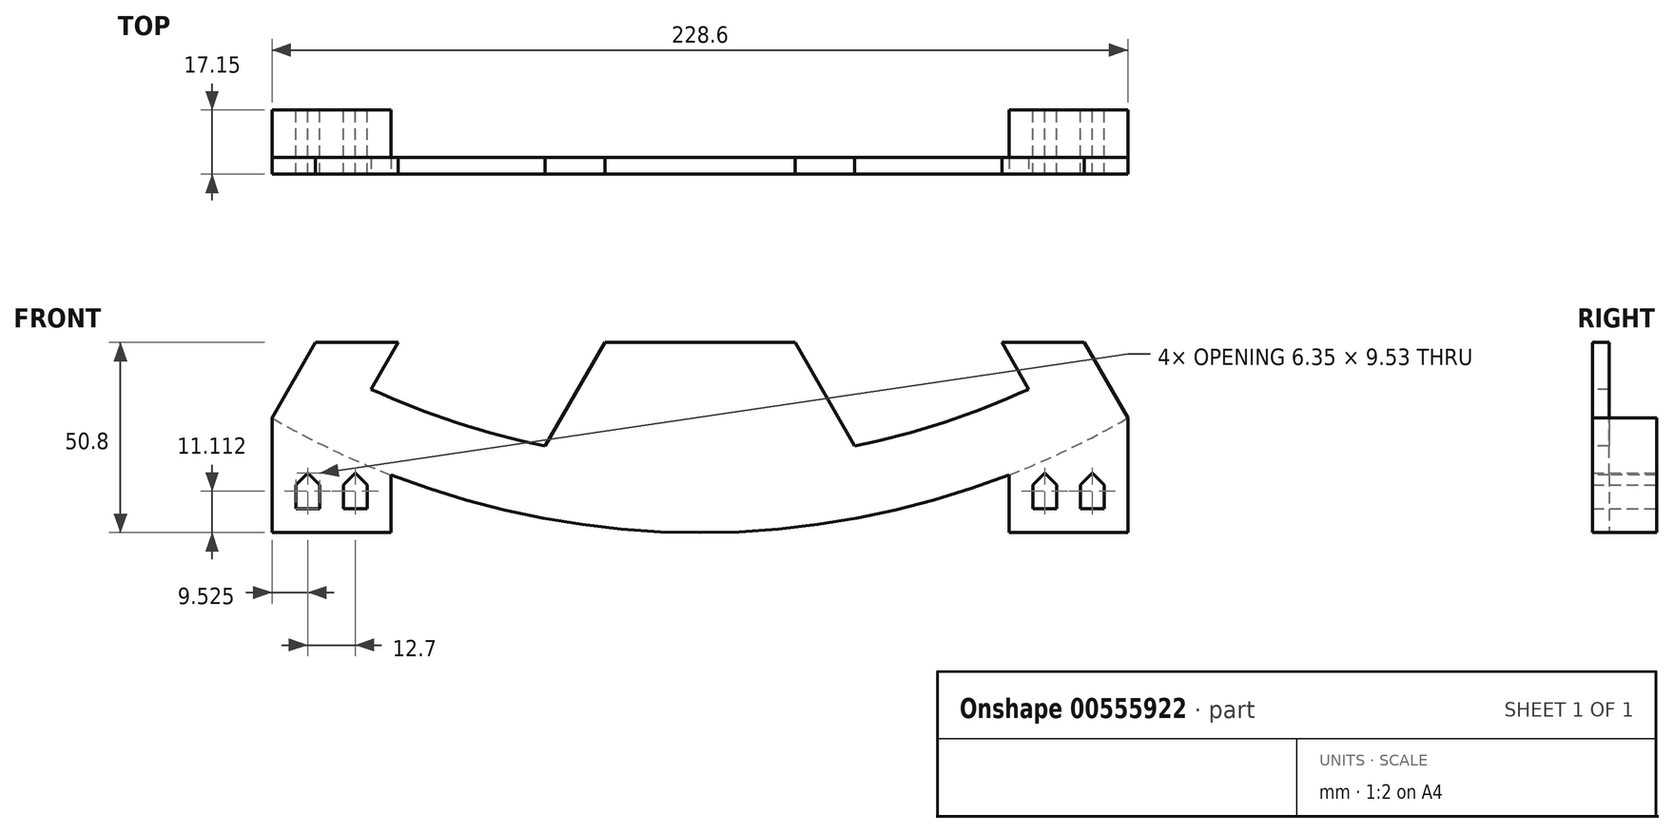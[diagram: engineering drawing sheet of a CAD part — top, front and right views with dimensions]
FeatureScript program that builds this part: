
annotation { "Feature Type Name" : "Feature", "Feature Type Description" : "" }
export const myFeature = defineFeature(function(context is Context, id is Id, definition is map)
    precondition{}
    {
        {
            var Q0;
            Q0=qCreatedBy(makeId("Front.planeOp"),FACE);
            var sketch = newSketch(context, id + "F0", { "sketchPlane" : qUnion([Q0])});
            skArc(sketch, "E0", {"start": v(-228.6, 0) * mm, "mid": v(0, -228.6) * mm, "end": v(228.6, 0) * mm});
            skLineSegment(sketch, "E1", {"start": v(-38.1, 0) * mm, "end": v(-228.6, 0) * mm});
            skLineSegment(sketch, "E2", {"start": v(38.1, 0) * mm, "end": v(228.6, 0) * mm});
            skLineSegment(sketch, "E3", {"start": v(-19.05, -33) * mm, "end": v(-114.3, -197.97) * mm});
            skLineSegment(sketch, "E4", {"start": v(19.05, -33) * mm, "end": v(114.3, -197.97) * mm});
            skArc(sketch, "E5", {"start": v(19.05, -33) * mm, "mid": v(0, 38.1) * mm, "end": v(-19.05, -33) * mm});
            skSolve(sketch);
        }
        {
            var Q0;
            {var subQ3=sQuery(id+"F0.wireOp",EDGE,"E3");Q0=makeQuery(id+"F0.imprint","IMPRINT",FACE,{"disambiguationData":[TD([[makeQuery(id+"F0.imprint","IMPRINT",EDGE,{"derivedFrom":subQ3}),1.0]])]});}
            extrude(context, id + "F1", {"entities" : qUnion([Q0]), "depth" : 127 * mm, "offsetDistance" : 25.4 * mm});
        }
        {
            var Q0;
            Q0=makeQuery(id+"F1.opExtrude","SWEPT_FACE",FACE,{"disambiguationData":[OSD([sQuery(id+"F0.wireOp",EDGE,"E5")])]});
            var Q1;
            Q1=makeQuery(id+"F1.opExtrude","SWEPT_FACE",FACE,{"disambiguationData":[OSD([sQuery(id+"F0.wireOp",EDGE,"E4")])]});
            var Q2;
            Q2=makeQuery(id+"F1.opExtrude","SWEPT_FACE",FACE,{"disambiguationData":[OSD([sQuery(id+"F0.wireOp",EDGE,"E3")])]});
            shell(context, id + "F2", {"entities" : qUnion([Q0, Q1, Q2]), "thickness" : 4.44 * mm});
        }
        {
            var Q0;
            Q0=makeQuery(id+"F1.opExtrude","CAP_FACE",FACE,{"disambiguationData":[OSD([sQuery(id+"F0.wireOp",EDGE,"E0"),sQuery(id+"F0.wireOp",EDGE,"E3"),sQuery(id+"F0.wireOp",EDGE,"E4"),sQuery(id+"F0.wireOp",EDGE,"E5")])],"isStart":false});
            var sketch = newSketch(context, id + "F3", { "sketchPlane" : qUnion([Q0])});
            skLineSegment(sketch, "E6.0", {"start": v(7.05, -50.3) * mm, "end": v(87.84, -190.25) * mm});
            skArc(sketch, "E6.1", {"start": v(-87.84, -190.25) * mm, "mid": v(-48.4, -203.88) * mm, "end": v(-7.05, -209.43) * mm});
            skCircle(sketch, "E7", {"center": v(0, 0) * mm, "radius": 9.53 * mm});
            skLineSegment(sketch, "E8", {"start": v(-7.05, -50.3) * mm, "end": v(-7.05, -125.9) * mm});
            skLineSegment(sketch, "E9", {"start": v(7.05, -50.3) * mm, "end": v(7.05, -125.9) * mm});
            skLineSegment(sketch, "E10", {"start": v(-87.84, -190.25) * mm, "end": v(-50.62, -125.78) * mm});
            skPoint(sketch, "E11.endSnap0", {"position": v(-66.67, -115.48) * mm});
            skLineSegment(sketch, "E12", {"start": v(-44.27, -114.78) * mm, "end": v(-14.9, -131.73) * mm});
            skLineSegment(sketch, "E13.trimOffspring", {"start": v(-7.05, -169.35) * mm, "end": v(-7.05, -209.43) * mm});
            skLineSegment(sketch, "E14.trimOffspring", {"start": v(-50.62, -125.78) * mm, "end": v(-87.84, -190.25) * mm});
            skArc(sketch, "E15.trimOffspring", {"start": v(7.05, -209.43) * mm, "mid": v(48.4, -203.88) * mm, "end": v(87.84, -190.25) * mm});
            skLineSegment(sketch, "E16", {"start": v(-7.05, -50.3) * mm, "end": v(0, -50.3) * mm, "construction": true});
            skLineSegment(sketch, "E17", {"start": v(0, -50.3) * mm, "end": v(0, -85.39) * mm, "construction": true});
            skLineSegment(sketch, "E18", {"start": v(-44.27, -114.78) * mm, "end": v(-7.05, -50.3) * mm});
            skLineSegment(sketch, "E19.MirrorCS", {"start": v(44.27, -114.78) * mm, "end": v(14.9, -131.73) * mm});
            skLineSegment(sketch, "E20.trimOffspring", {"start": v(7.05, -169.35) * mm, "end": v(7.05, -209.43) * mm});
            skArc(sketch, "E21", {"start": v(14.9, -131.73) * mm, "mid": v(11.36, -128.3) * mm, "end": v(7.05, -125.9) * mm});
            skPoint(sketch, "E22.orphan", {"position": v(7.05, -136.27) * mm});
            skPoint(sketch, "E23.orphan", {"position": v(7.05, -150.93) * mm});
            skPoint(sketch, "E24.orphan", {"position": v(-7.05, -150.93) * mm});
            skPoint(sketch, "E25.orphan", {"position": v(-7.05, -136.27) * mm});
            skLineSegment(sketch, "E26", {"start": v(50.62, -125.78) * mm, "end": v(7.05, -169.35) * mm, "construction": true});
            skLineSegment(sketch, "E27", {"start": v(50.62, -125.78) * mm, "end": v(7.05, -169.35) * mm});
            skLineSegment(sketch, "E28.MirrorCS", {"start": v(-50.62, -125.78) * mm, "end": v(-7.05, -169.35) * mm});
            skArc(sketch, "E29.trimOffspring", {"start": v(-7.05, -125.9) * mm, "mid": v(-11.36, -128.3) * mm, "end": v(-14.9, -131.73) * mm});
            skSolve(sketch);
        }
        {
            var Q0;
            Q0=makeQuery(id+"F3.imprint","IMPRINT",FACE,{"disambiguationData":[TD([[makeQuery(id+"F3.imprint","IMPRINT",EDGE,{"derivedFrom":sQuery(id+"F3.wireOp",EDGE,"E6.1")}),1.0]])]});
            var Q1;
            {var subQ2=sQuery(id+"F3.wireOp",EDGE,"E15.trimOffspring");Q1=makeQuery(id+"F3.imprint","IMPRINT",FACE,{"disambiguationData":[TD([[makeQuery(id+"F3.imprint","IMPRINT",EDGE,{"derivedFrom":subQ2}),1.0]])]});}
            var Q2;
            {var subQ0=sQuery(id+"F3.wireOp",EDGE,"E9");Q2=makeQuery(id+"F3.imprint","IMPRINT",FACE,{"disambiguationData":[TD([[makeQuery(id+"F3.imprint","IMPRINT",EDGE,{"derivedFrom":subQ0}),1.0]])]});}
            var Q3;
            {var subQ0=sQuery(id+"F3.wireOp",EDGE,"E8");Q3=makeQuery(id+"F3.imprint","IMPRINT",FACE,{"disambiguationData":[TD([[makeQuery(id+"F3.imprint","IMPRINT",EDGE,{"derivedFrom":subQ0}),-1.0]])]});}
            var Q4;
            Q4=makeQuery(id+"F3.imprint","IMPRINT",FACE,{"disambiguationData":[TD([[makeQuery(id+"F3.imprint","IMPRINT",EDGE,{"derivedFrom":sQuery(id+"F3.wireOp",EDGE,"E7")}),1.0]])]});
            var Q5;
            Q5=makeQuery(id+"F1.opExtrude","CAP_FACE",FACE,{"disambiguationData":[OSD([sQuery(id+"F0.wireOp",EDGE,"E0"),sQuery(id+"F0.wireOp",EDGE,"E3"),sQuery(id+"F0.wireOp",EDGE,"E4"),sQuery(id+"F0.wireOp",EDGE,"E5")])],"isStart":true});
            extrude(context, id + "F4", {"entities" : qUnion([Q0, Q1, Q2, Q3, Q4]), "operationType" : NewBodyOperationType.REMOVE, "endBound" : BoundingType.UP_TO_SURFACE, "oppositeDirection" : true, "depth" : 25.4 * mm, "endBoundEntityFace" : qUnion([Q5]), "offsetDistance" : 25.4 * mm});
        }
        {
            var Q0;
            Q0=qCreatedBy(makeId("Front.planeOp"),FACE);
            var sketch = newSketch(context, id + "F5", { "sketchPlane" : qUnion([Q0])});
            skLineSegment(sketch, "E30", {"start": v(0, -228.6) * mm, "end": v(114.3, -228.6) * mm});
            skLineSegment(sketch, "E31", {"start": v(0, -228.6) * mm, "end": v(-114.3, -228.6) * mm});
            skLineSegment(sketch, "E32", {"start": v(114.3, -197.97) * mm, "end": v(114.3, -228.6) * mm});
            skLineSegment(sketch, "E33", {"start": v(-114.3, -197.97) * mm, "end": v(-114.3, -228.6) * mm});
            skPoint(sketch, "E34.orphan", {"position": v(-122.47, -228.6) * mm});
            skArc(sketch, "E35.0", {"start": v(-114.3, -197.97) * mm, "mid": v(0, -228.6) * mm, "end": v(114.3, -197.97) * mm});
            skLineSegment(sketch, "E36", {"start": v(114.3, -228.6) * mm, "end": v(107.95, -228.6) * mm, "construction": true});
            skLineSegment(sketch, "E37", {"start": v(107.95, -228.6) * mm, "end": v(107.95, -222.25) * mm, "construction": true});
            skLineSegment(sketch, "E38.bottom", {"start": v(107.95, -222.25) * mm, "end": v(101.6, -222.25) * mm});
            skLineSegment(sketch, "E38.left", {"start": v(107.95, -222.25) * mm, "end": v(107.95, -215.9) * mm});
            skLineSegment(sketch, "E38.right", {"start": v(88.9, -222.25) * mm, "end": v(88.9, -215.9) * mm});
            skLineSegment(sketch, "E39", {"start": v(101.6, -222.25) * mm, "end": v(101.6, -215.9) * mm});
            skLineSegment(sketch, "E40", {"start": v(95.25, -222.25) * mm, "end": v(95.25, -215.9) * mm});
            skLineSegment(sketch, "E41.trimOffspring", {"start": v(95.25, -222.25) * mm, "end": v(88.9, -222.25) * mm});
            skLineSegment(sketch, "E42", {"start": v(104.78, -215.9) * mm, "end": v(104.78, -212.72) * mm, "construction": true});
            skLineSegment(sketch, "E43", {"start": v(92.08, -215.9) * mm, "end": v(92.08, -212.72) * mm, "construction": true});
            skLineSegment(sketch, "E44", {"start": v(107.95, -215.9) * mm, "end": v(104.78, -212.72) * mm});
            skLineSegment(sketch, "E45", {"start": v(101.6, -215.9) * mm, "end": v(104.78, -212.72) * mm});
            skLineSegment(sketch, "E46", {"start": v(95.25, -215.9) * mm, "end": v(92.08, -212.72) * mm});
            skLineSegment(sketch, "E47", {"start": v(88.9, -215.9) * mm, "end": v(92.08, -212.72) * mm});
            skLineSegment(sketch, "E48.MirrorCS", {"start": v(-104.78, -215.9) * mm, "end": v(-104.78, -212.72) * mm, "construction": true});
            skLineSegment(sketch, "E49.MirrorCS", {"start": v(-92.08, -215.9) * mm, "end": v(-92.08, -212.72) * mm, "construction": true});
            skLineSegment(sketch, "E50.MirrorCS", {"start": v(-101.6, -215.9) * mm, "end": v(-104.78, -212.72) * mm});
            skLineSegment(sketch, "E51.MirrorCS", {"start": v(-88.9, -215.9) * mm, "end": v(-92.08, -212.72) * mm});
            skLineSegment(sketch, "E52.MirrorCS", {"start": v(-107.95, -215.9) * mm, "end": v(-104.78, -212.72) * mm});
            skLineSegment(sketch, "E53.MirrorCS", {"start": v(-95.25, -222.25) * mm, "end": v(-95.25, -215.9) * mm});
            skLineSegment(sketch, "E54.MirrorCS", {"start": v(-101.6, -222.25) * mm, "end": v(-101.6, -215.9) * mm});
            skLineSegment(sketch, "E55.MirrorCS", {"start": v(-107.95, -222.25) * mm, "end": v(-107.95, -215.9) * mm});
            skLineSegment(sketch, "E56.MirrorCS", {"start": v(-107.95, -222.25) * mm, "end": v(-101.6, -222.25) * mm});
            skLineSegment(sketch, "E57.MirrorCS", {"start": v(-88.9, -222.25) * mm, "end": v(-88.9, -215.9) * mm});
            skLineSegment(sketch, "E58.MirrorCS", {"start": v(-95.25, -215.9) * mm, "end": v(-92.08, -212.72) * mm});
            skLineSegment(sketch, "E59.MirrorCS", {"start": v(-95.25, -222.25) * mm, "end": v(-88.9, -222.25) * mm});
            skSolve(sketch);
        }
        {
            var Q0;
            {var subQ2=sQuery(id+"F5.wireOp",EDGE,"E30");Q0=makeQuery(id+"F5.imprint","IMPRINT",FACE,{"disambiguationData":[TD([[makeQuery(id+"F5.imprint","IMPRINT",EDGE,{"derivedFrom":subQ2}),1.0]])]});}
            var Q1;
            {var subQ2=sQuery(id+"F5.wireOp",EDGE,"E31");Q1=makeQuery(id+"F5.imprint","IMPRINT",FACE,{"disambiguationData":[TD([[makeQuery(id+"F5.imprint","IMPRINT",EDGE,{"derivedFrom":subQ2}),-1.0]])]});}
            var Q2;
            Q2=makeQuery(id+"F1.opExtrude","CAP_FACE",FACE,{"disambiguationData":[OSD([sQuery(id+"F0.wireOp",EDGE,"E0"),sQuery(id+"F0.wireOp",EDGE,"E3"),sQuery(id+"F0.wireOp",EDGE,"E4"),sQuery(id+"F0.wireOp",EDGE,"E5")])],"isStart":false});
            extrude(context, id + "F6", {"entities" : qUnion([Q0, Q1]), "operationType" : NewBodyOperationType.ADD, "endBound" : BoundingType.UP_TO_SURFACE, "depth" : 25.4 * mm, "endBoundEntityFace" : qUnion([Q2]), "offsetDistance" : 25.4 * mm});
        }
        {
            var Q0;
            Q0=qCreatedBy(makeId("Front.planeOp"),FACE);
            var sketch = newSketch(context, id + "F7", { "sketchPlane" : qUnion([Q0])});
            skLineSegment(sketch, "E60", {"start": v(0, 0) * mm, "end": v(0, -177.8) * mm, "construction": true});
            skLineSegment(sketch, "E61", {"start": v(0, -177.8) * mm, "end": v(122.5, -177.8) * mm});
            skLineSegment(sketch, "E62", {"start": v(122.5, -177.8) * mm, "end": v(122.5, 99.95) * mm});
            skLineSegment(sketch, "E63", {"start": v(0, -177.8) * mm, "end": v(-155.13, -177.8) * mm});
            skLineSegment(sketch, "E64", {"start": v(-155.13, -177.8) * mm, "end": v(-155.13, 97.68) * mm});
            skLineSegment(sketch, "E65", {"start": v(-155.13, 97.68) * mm, "end": v(122.5, 99.95) * mm});
            skSolve(sketch);
        }
        {
            var Q0;
            Q0=makeQuery(id+"F7.imprint","IMPRINT",FACE,{"disambiguationData":[TD([[makeQuery(id+"F7.imprint","IMPRINT",EDGE,{"derivedFrom":sQuery(id+"F7.wireOp",EDGE,"E61")}),1.0]])]});
            extrude(context, id + "F8", {"entities" : qUnion([Q0]), "operationType" : NewBodyOperationType.REMOVE, "depth" : 154.94 * mm, "offsetDistance" : 25.4 * mm});
        }
        {
            var Q0;
            {var subQ0=sQuery(id+"F5.wireOp",EDGE,"E35.0");Q0=makeQuery(id+"F6.boolean.opBoolean","MERGE",FACE,{"derivedFrom":[makeQuery(id+"F1.opExtrude","CAP_FACE",FACE,{"disambiguationData":[OSD([sQuery(id+"F0.wireOp",EDGE,"E0"),sQuery(id+"F0.wireOp",EDGE,"E3"),sQuery(id+"F0.wireOp",EDGE,"E4"),sQuery(id+"F0.wireOp",EDGE,"E5")])],"isStart":true}),makeQuery(id+"F6.opExtrude","CAP_FACE",FACE,{"disambiguationData":[OSD([sQuery(id+"F5.wireOp",EDGE,"E30"),sQuery(id+"F5.wireOp",EDGE,"E32"),subQ0,sQuery(id+"F5.wireOp",EDGE,"E38.bottom"),sQuery(id+"F5.wireOp",EDGE,"E38.left"),sQuery(id+"F5.wireOp",EDGE,"E38.right"),sQuery(id+"F5.wireOp",EDGE,"E39"),sQuery(id+"F5.wireOp",EDGE,"E40"),sQuery(id+"F5.wireOp",EDGE,"E41.trimOffspring"),sQuery(id+"F5.wireOp",EDGE,"E44"),sQuery(id+"F5.wireOp",EDGE,"E45"),sQuery(id+"F5.wireOp",EDGE,"E46"),sQuery(id+"F5.wireOp",EDGE,"E47")])],"isStart":true}),makeQuery(id+"F6.opExtrude","CAP_FACE",FACE,{"disambiguationData":[OSD([sQuery(id+"F5.wireOp",EDGE,"E31"),sQuery(id+"F5.wireOp",EDGE,"E33"),subQ0,sQuery(id+"F5.wireOp",EDGE,"E50.MirrorCS"),sQuery(id+"F5.wireOp",EDGE,"E51.MirrorCS"),sQuery(id+"F5.wireOp",EDGE,"E52.MirrorCS"),sQuery(id+"F5.wireOp",EDGE,"E53.MirrorCS"),sQuery(id+"F5.wireOp",EDGE,"E54.MirrorCS"),sQuery(id+"F5.wireOp",EDGE,"E55.MirrorCS"),sQuery(id+"F5.wireOp",EDGE,"E56.MirrorCS"),sQuery(id+"F5.wireOp",EDGE,"E57.MirrorCS"),sQuery(id+"F5.wireOp",EDGE,"E58.MirrorCS"),sQuery(id+"F5.wireOp",EDGE,"E59.MirrorCS")])],"isStart":true})]});}
            var sketch = newSketch(context, id + "F9", { "sketchPlane" : qUnion([Q0])});
            skArc(sketch, "E66.0", {"start": v(-87.84, -190.25) * mm, "mid": v(-48.4, -203.88) * mm, "end": v(-7.05, -209.43) * mm});
            skLineSegment(sketch, "E67.0", {"start": v(-7.05, -209.43) * mm, "end": v(-7.05, -177.8) * mm});
            skLineSegment(sketch, "E68", {"start": v(0, -177.8) * mm, "end": v(25.4, -177.8) * mm});
            skLineSegment(sketch, "E69", {"start": v(0, -177.8) * mm, "end": v(-25.4, -177.8) * mm});
            skLineSegment(sketch, "E70", {"start": v(-25.4, -177.8) * mm, "end": v(-41.35, -205.43) * mm});
            skLineSegment(sketch, "E71", {"start": v(25.4, -177.8) * mm, "end": v(41.35, -205.43) * mm});
            skLineSegment(sketch, "E72.0", {"start": v(7.05, -209.43) * mm, "end": v(7.05, -177.8) * mm});
            skArc(sketch, "E73.0", {"start": v(7.05, -209.43) * mm, "mid": v(48.4, -203.88) * mm, "end": v(87.84, -190.25) * mm});
            skSolve(sketch);
        }
        {
            var Q0;
            {var subQ0=sQuery(id+"F9.wireOp",EDGE,"E67.0");Q0=makeQuery(id+"F9.imprint","IMPRINT",FACE,{"disambiguationData":[TD([[makeQuery(id+"F9.imprint","IMPRINT",EDGE,{"derivedFrom":subQ0}),1.0]])]});}
            var Q1;
            {var subQ2=sQuery(id+"F9.wireOp",EDGE,"E71");Q1=makeQuery(id+"F9.imprint","IMPRINT",FACE,{"disambiguationData":[TD([[makeQuery(id+"F9.imprint","IMPRINT",EDGE,{"derivedFrom":subQ2}),-1.0]])]});}
            var Q2;
            {var subQ0=sQuery(id+"F0.wireOp",EDGE,"E5");var subQ1=sQuery(id+"F0.wireOp",EDGE,"E4");var subQ2=sQuery(id+"F0.wireOp",EDGE,"E3");var subQ3=sQuery(id+"F0.wireOp",EDGE,"E0");Q2=makeQuery(id+"F2.opShell","OFFSET_FACE",FACE,{"disambiguationData":[OSD([subQ3,subQ2,subQ1,subQ0]),TDD([makeQuery(id+"F1.opExtrude","CAP_FACE",FACE,{"disambiguationData":[OSD([subQ3,subQ2,subQ1,subQ0])],"isStart":true})])]});}
            extrude(context, id + "F10", {"entities" : qUnion([Q0, Q1]), "operationType" : NewBodyOperationType.ADD, "endBound" : BoundingType.UP_TO_SURFACE, "oppositeDirection" : true, "depth" : 25.4 * mm, "endBoundEntityFace" : qUnion([Q2]), "offsetDistance" : 25.4 * mm});
        }
        {
            var Q0;
            Q0=qCreatedBy(makeId("Front.planeOp"),FACE);
            var Q1;
            {var subQ0=sQuery(id+"F0.wireOp",EDGE,"E5");var subQ1=sQuery(id+"F0.wireOp",EDGE,"E4");var subQ2=sQuery(id+"F0.wireOp",EDGE,"E3");var subQ3=sQuery(id+"F0.wireOp",EDGE,"E0");Q1=makeQuery(id+"F6.boolean.opBoolean","MERGE",FACE,{"derivedFrom":[makeQuery(id+"F1.opExtrude","CAP_FACE",FACE,{"disambiguationData":[OSD([subQ3,subQ2,subQ1,subQ0])],"isStart":false}),makeQuery(id+"F6.opExtrude","CAP_FACE",FACE,{"disambiguationData":[OSD([subQ3,subQ2,subQ1,subQ0]),OD(0.0)],"isStart":false}),makeQuery(id+"F6.opExtrude","CAP_FACE",FACE,{"disambiguationData":[OSD([subQ3,subQ2,subQ1,subQ0]),OD(1.0)],"isStart":false})]});}
            cPlane(context, id + "F11", {"entities" : qUnion([Q0, Q1]), "cplaneType" : CPlaneType.MID_PLANE, "offset" : 25.4 * mm, "width" : 152.4 * mm, "height" : 152.4 * mm});
        }
        {
            var Q0;
            Q0=makeQuery(id+"F1.opExtrude","SWEPT_BODY",BODY,{"disambiguationData":[OSD([sQuery(id+"F0.wireOp",EDGE,"E0"),sQuery(id+"F0.wireOp",EDGE,"E3"),sQuery(id+"F0.wireOp",EDGE,"E4"),sQuery(id+"F0.wireOp",EDGE,"E5")])]});
            var Q1;
            Q1=qCreatedBy(id+"F11.planeOp",FACE);
            mirror(context, id + "F12", {"operationType" : NewBodyOperationType.ADD, "entities" : qUnion([Q0]), "mirrorPlane" : qUnion([Q1])});
        }
        {
            var Q0;
            {var subQ0=sQuery(id+"F5.wireOp",EDGE,"E35.0");var subQ1=sQuery(id+"F0.wireOp",EDGE,"E5");var subQ2=sQuery(id+"F0.wireOp",EDGE,"E4");var subQ3=sQuery(id+"F0.wireOp",EDGE,"E3");var subQ4=sQuery(id+"F0.wireOp",EDGE,"E0");Q0=makeQuery(id+"F12.boolean.opBoolean","MERGE",FACE,{"derivedFrom":[makeQuery(id+"F6.boolean.opBoolean","MERGE",FACE,{"derivedFrom":[makeQuery(id+"F1.opExtrude","CAP_FACE",FACE,{"disambiguationData":[OSD([subQ4,subQ3,subQ2,subQ1])],"isStart":false}),makeQuery(id+"F6.opExtrude","CAP_FACE",FACE,{"disambiguationData":[OSD([subQ4,subQ3,subQ2,subQ1]),OD(0.0)],"isStart":false}),makeQuery(id+"F6.opExtrude","CAP_FACE",FACE,{"disambiguationData":[OSD([subQ4,subQ3,subQ2,subQ1]),OD(1.0)],"isStart":false})]}),makeQuery(id+"F12.opPattern","COPY",FACE,{"derivedFrom":makeQuery(id+"F10.boolean.opBoolean","MERGE",FACE,{"derivedFrom":[makeQuery(id+"F6.boolean.opBoolean","MERGE",FACE,{"derivedFrom":[makeQuery(id+"F1.opExtrude","CAP_FACE",FACE,{"disambiguationData":[OSD([subQ4,subQ3,subQ2,subQ1])],"isStart":true}),makeQuery(id+"F6.opExtrude","CAP_FACE",FACE,{"disambiguationData":[OSD([sQuery(id+"F5.wireOp",EDGE,"E30"),sQuery(id+"F5.wireOp",EDGE,"E32"),subQ0,sQuery(id+"F5.wireOp",EDGE,"E38.bottom"),sQuery(id+"F5.wireOp",EDGE,"E38.left"),sQuery(id+"F5.wireOp",EDGE,"E38.right"),sQuery(id+"F5.wireOp",EDGE,"E39"),sQuery(id+"F5.wireOp",EDGE,"E40"),sQuery(id+"F5.wireOp",EDGE,"E41.trimOffspring"),sQuery(id+"F5.wireOp",EDGE,"E44"),sQuery(id+"F5.wireOp",EDGE,"E45"),sQuery(id+"F5.wireOp",EDGE,"E46"),sQuery(id+"F5.wireOp",EDGE,"E47")])],"isStart":true}),makeQuery(id+"F6.opExtrude","CAP_FACE",FACE,{"disambiguationData":[OSD([sQuery(id+"F5.wireOp",EDGE,"E31"),sQuery(id+"F5.wireOp",EDGE,"E33"),subQ0,sQuery(id+"F5.wireOp",EDGE,"E50.MirrorCS"),sQuery(id+"F5.wireOp",EDGE,"E51.MirrorCS"),sQuery(id+"F5.wireOp",EDGE,"E52.MirrorCS"),sQuery(id+"F5.wireOp",EDGE,"E53.MirrorCS"),sQuery(id+"F5.wireOp",EDGE,"E54.MirrorCS"),sQuery(id+"F5.wireOp",EDGE,"E55.MirrorCS"),sQuery(id+"F5.wireOp",EDGE,"E56.MirrorCS"),sQuery(id+"F5.wireOp",EDGE,"E57.MirrorCS"),sQuery(id+"F5.wireOp",EDGE,"E58.MirrorCS"),sQuery(id+"F5.wireOp",EDGE,"E59.MirrorCS")])],"isStart":true})]}),makeQuery(id+"F10.opExtrude","CAP_FACE",FACE,{"disambiguationData":[OSD([sQuery(id+"F9.wireOp",EDGE,"E66.0"),sQuery(id+"F9.wireOp",EDGE,"E67.0"),sQuery(id+"F9.wireOp",EDGE,"E69"),sQuery(id+"F9.wireOp",EDGE,"E70")])],"isStart":true}),makeQuery(id+"F10.opExtrude","CAP_FACE",FACE,{"disambiguationData":[OSD([sQuery(id+"F9.wireOp",EDGE,"E68"),sQuery(id+"F9.wireOp",EDGE,"E71"),sQuery(id+"F9.wireOp",EDGE,"E72.0"),sQuery(id+"F9.wireOp",EDGE,"E73.0")])],"isStart":true})]}),"instanceName":"1"})]});}
            var sketch = newSketch(context, id + "F13", { "sketchPlane" : qUnion([Q0])});
            skArc(sketch, "E74", {"start": v(-114.3, -197.97) * mm, "mid": v(0, -228.6) * mm, "end": v(114.3, -197.97) * mm});
            skLineSegment(sketch, "E75.0", {"start": v(114.3, -228.6) * mm, "end": v(-114.3, -228.6) * mm});
            skLineSegment(sketch, "E76", {"start": v(-82.55, -228.6) * mm, "end": v(-82.55, -213.17) * mm});
            skLineSegment(sketch, "E77.MirrorCS", {"start": v(82.55, -228.6) * mm, "end": v(82.55, -213.17) * mm});
            skArc(sketch, "E78.MirrorCS", {"start": v(114.3, -197.97) * mm, "mid": v(0, -228.6) * mm, "end": v(-114.3, -197.97) * mm});
            skLineSegment(sketch, "E79.MirrorCS", {"start": v(-114.3, -228.6) * mm, "end": v(114.3, -228.6) * mm});
            skSolve(sketch);
        }
        {
            var Q0;
            {var subQ0=sQuery(id+"F13.wireOp",EDGE,"E76");Q0=makeQuery(id+"F13.imprint","IMPRINT",FACE,{"disambiguationData":[TD([[makeQuery(id+"F13.imprint","IMPRINT",EDGE,{"derivedFrom":subQ0}),-1.0]])]});}
            var Q1;
            {var subQ0=sQuery(id+"F13.wireOp",EDGE,"E77.MirrorCS");Q1=makeQuery(id+"F13.imprint","IMPRINT",FACE,{"disambiguationData":[TD([[makeQuery(id+"F13.imprint","IMPRINT",EDGE,{"derivedFrom":subQ0}),1.0]])]});}
            var Q2;
            {var subQ0=sQuery(id+"F5.wireOp",EDGE,"E35.0");Q2=makeQuery(id+"F10.boolean.opBoolean","MERGE",FACE,{"derivedFrom":[makeQuery(id+"F6.boolean.opBoolean","MERGE",FACE,{"derivedFrom":[makeQuery(id+"F1.opExtrude","CAP_FACE",FACE,{"disambiguationData":[OSD([sQuery(id+"F0.wireOp",EDGE,"E0"),sQuery(id+"F0.wireOp",EDGE,"E3"),sQuery(id+"F0.wireOp",EDGE,"E4"),sQuery(id+"F0.wireOp",EDGE,"E5")])],"isStart":true}),makeQuery(id+"F6.opExtrude","CAP_FACE",FACE,{"disambiguationData":[OSD([sQuery(id+"F5.wireOp",EDGE,"E30"),sQuery(id+"F5.wireOp",EDGE,"E32"),subQ0,sQuery(id+"F5.wireOp",EDGE,"E38.bottom"),sQuery(id+"F5.wireOp",EDGE,"E38.left"),sQuery(id+"F5.wireOp",EDGE,"E38.right"),sQuery(id+"F5.wireOp",EDGE,"E39"),sQuery(id+"F5.wireOp",EDGE,"E40"),sQuery(id+"F5.wireOp",EDGE,"E41.trimOffspring"),sQuery(id+"F5.wireOp",EDGE,"E44"),sQuery(id+"F5.wireOp",EDGE,"E45"),sQuery(id+"F5.wireOp",EDGE,"E46"),sQuery(id+"F5.wireOp",EDGE,"E47")])],"isStart":true}),makeQuery(id+"F6.opExtrude","CAP_FACE",FACE,{"disambiguationData":[OSD([sQuery(id+"F5.wireOp",EDGE,"E31"),sQuery(id+"F5.wireOp",EDGE,"E33"),subQ0,sQuery(id+"F5.wireOp",EDGE,"E50.MirrorCS"),sQuery(id+"F5.wireOp",EDGE,"E51.MirrorCS"),sQuery(id+"F5.wireOp",EDGE,"E52.MirrorCS"),sQuery(id+"F5.wireOp",EDGE,"E53.MirrorCS"),sQuery(id+"F5.wireOp",EDGE,"E54.MirrorCS"),sQuery(id+"F5.wireOp",EDGE,"E55.MirrorCS"),sQuery(id+"F5.wireOp",EDGE,"E56.MirrorCS"),sQuery(id+"F5.wireOp",EDGE,"E57.MirrorCS"),sQuery(id+"F5.wireOp",EDGE,"E58.MirrorCS"),sQuery(id+"F5.wireOp",EDGE,"E59.MirrorCS")])],"isStart":true})]}),makeQuery(id+"F10.opExtrude","CAP_FACE",FACE,{"disambiguationData":[OSD([sQuery(id+"F9.wireOp",EDGE,"E66.0"),sQuery(id+"F9.wireOp",EDGE,"E67.0"),sQuery(id+"F9.wireOp",EDGE,"E69"),sQuery(id+"F9.wireOp",EDGE,"E70")])],"isStart":true}),makeQuery(id+"F10.opExtrude","CAP_FACE",FACE,{"disambiguationData":[OSD([sQuery(id+"F9.wireOp",EDGE,"E68"),sQuery(id+"F9.wireOp",EDGE,"E71"),sQuery(id+"F9.wireOp",EDGE,"E72.0"),sQuery(id+"F9.wireOp",EDGE,"E73.0")])],"isStart":true})]});}
            extrude(context, id + "F14", {"entities" : qUnion([Q0, Q1]), "operationType" : NewBodyOperationType.REMOVE, "endBound" : BoundingType.UP_TO_SURFACE, "oppositeDirection" : true, "depth" : 25.4 * mm, "endBoundEntityFace" : qUnion([Q2]), "offsetDistance" : 25.4 * mm});
        }
        {
            var Q0;
            Q0=qCreatedBy(makeId("Top.planeOp"),FACE);
            var sketch = newSketch(context, id + "F15", { "sketchPlane" : qUnion([Q0])});
            skPoint(sketch, "E80.0", {"position": v(-112.08, -4.45) * mm});
            skPoint(sketch, "E81.0", {"position": v(112.08, -4.45) * mm});
            skPoint(sketch, "E82.0", {"position": v(112.08, -122.55) * mm});
            skPoint(sketch, "E83.0", {"position": v(-112.08, -122.55) * mm});
            skLineSegment(sketch, "E84.0", {"start": v(-114.3, -122.55) * mm, "end": v(-114.3, -4.45) * mm});
            skLineSegment(sketch, "E85.0", {"start": v(114.3, -122.55) * mm, "end": v(114.3, -4.45) * mm});
            skLineSegment(sketch, "E86", {"start": v(114.3, -122.55) * mm, "end": v(-114.3, -122.55) * mm});
            skPoint(sketch, "E87.orphan", {"position": v(114.3, -127) * mm});
            skPoint(sketch, "E88.orphan", {"position": v(-114.3, -127) * mm});
            skPoint(sketch, "E89.orphan", {"position": v(114.3, 0) * mm});
            skPoint(sketch, "E90.orphan", {"position": v(-114.3, 0) * mm});
            skLineSegment(sketch, "E91", {"start": v(-114.3, -4.45) * mm, "end": v(-114.3, 0) * mm});
            skLineSegment(sketch, "E92", {"start": v(-114.3, 0) * mm, "end": v(114.3, 0) * mm});
            skLineSegment(sketch, "E93", {"start": v(114.3, 0) * mm, "end": v(114.3, -4.45) * mm});
            skSolve(sketch);
        }
        {
            var Q0;
            Q0 = qSketchRegion(id + "F15", true);
            extrude(context, id + "F16", {"entities" : qUnion([Q0]), "operationType" : NewBodyOperationType.REMOVE, "oppositeDirection" : true, "depth" : 279.4 * mm, "offsetDistance" : 25.4 * mm});
        }
        {
            var Q0;
            {var subQ0=sQuery(id+"F0.wireOp",EDGE,"E5");var subQ1=sQuery(id+"F0.wireOp",EDGE,"E4");var subQ2=sQuery(id+"F0.wireOp",EDGE,"E3");var subQ3=sQuery(id+"F0.wireOp",EDGE,"E0");Q0=makeQuery(id+"F16.boolean.opBoolean","MERGE",FACE,{"derivedFrom":[makeQuery(id+"F12.boolean.opBoolean","MERGE",FACE,{"derivedFrom":[makeQuery(id+"F2.opShell","OFFSET_FACE",FACE,{"disambiguationData":[OSD([subQ3,subQ2,subQ1,subQ0]),TDD([makeQuery(id+"F1.opExtrude","CAP_FACE",FACE,{"disambiguationData":[OSD([subQ3,subQ2,subQ1,subQ0])],"isStart":false})])]}),makeQuery(id+"F12.opPattern","COPY",FACE,{"derivedFrom":makeQuery(id+"F10.boolean.opBoolean","MERGE",FACE,{"derivedFrom":[makeQuery(id+"F2.opShell","OFFSET_FACE",FACE,{"disambiguationData":[OSD([subQ3,subQ2,subQ1,subQ0]),TDD([makeQuery(id+"F1.opExtrude","CAP_FACE",FACE,{"disambiguationData":[OSD([subQ3,subQ2,subQ1,subQ0])],"isStart":true})])]}),makeQuery(id+"F10.opExtrude","CAP_FACE",FACE,{"disambiguationData":[OSD([subQ3,subQ2,subQ1,subQ0]),OD(0.0)],"isStart":false}),makeQuery(id+"F10.opExtrude","CAP_FACE",FACE,{"disambiguationData":[OSD([subQ3,subQ2,subQ1,subQ0]),OD(1.0)],"isStart":false})]}),"instanceName":"1"})]}),makeQuery(id+"F16.opExtrude","SWEPT_FACE",FACE,{"disambiguationData":[OSD([sQuery(id+"F15.wireOp",EDGE,"E86")])]})]});}
            var sketch = newSketch(context, id + "F17", { "sketchPlane" : qUnion([Q0])});
            skArc(sketch, "E94", {"start": v(-114.3, -197.97) * mm, "mid": v(-98.72, -206.19) * mm, "end": v(-82.55, -213.17) * mm});
            skLineSegment(sketch, "E95.0", {"start": v(-82.55, -228.6) * mm, "end": v(-114.3, -228.6) * mm});
            skLineSegment(sketch, "E96.0", {"start": v(-114.3, -228.6) * mm, "end": v(-114.3, -197.97) * mm});
            skLineSegment(sketch, "E97.0", {"start": v(-82.55, -228.6) * mm, "end": v(-82.55, -213.17) * mm});
            skPoint(sketch, "E98.0", {"position": v(-92.08, -222.25) * mm});
            skLineSegment(sketch, "E99.0", {"start": v(-95.25, -215.9) * mm, "end": v(-95.25, -222.25) * mm});
            skPoint(sketch, "E100.0", {"position": v(-93.66, -214.31) * mm});
            skLineSegment(sketch, "E101.0", {"start": v(-92.08, -212.72) * mm, "end": v(-88.9, -215.9) * mm});
            skLineSegment(sketch, "E102.0", {"start": v(-88.9, -215.9) * mm, "end": v(-88.9, -222.25) * mm});
            skPoint(sketch, "E103.0", {"position": v(-103.19, -214.31) * mm});
            skLineSegment(sketch, "E104.0", {"start": v(-104.78, -212.72) * mm, "end": v(-101.6, -215.9) * mm});
            skLineSegment(sketch, "E105.0", {"start": v(-104.78, -212.72) * mm, "end": v(-107.95, -215.9) * mm});
            skLineSegment(sketch, "E106.0", {"start": v(-107.95, -215.9) * mm, "end": v(-107.95, -222.25) * mm});
            skLineSegment(sketch, "E107.0", {"start": v(-101.6, -222.25) * mm, "end": v(-107.95, -222.25) * mm});
            skLineSegment(sketch, "E108.0", {"start": v(-101.6, -215.9) * mm, "end": v(-101.6, -222.25) * mm});
            skLineSegment(sketch, "E109.MirrorCS", {"start": v(101.6, -222.25) * mm, "end": v(107.95, -222.25) * mm});
            skLineSegment(sketch, "E110.MirrorCS", {"start": v(104.78, -212.72) * mm, "end": v(107.95, -215.9) * mm});
            skLineSegment(sketch, "E111.MirrorCS", {"start": v(101.6, -215.9) * mm, "end": v(101.6, -222.25) * mm});
            skLineSegment(sketch, "E112.MirrorCS", {"start": v(107.95, -215.9) * mm, "end": v(107.95, -222.25) * mm});
            skLineSegment(sketch, "E113.MirrorCS", {"start": v(104.78, -212.72) * mm, "end": v(101.6, -215.9) * mm});
            skLineSegment(sketch, "E114.MirrorCS", {"start": v(92.08, -212.72) * mm, "end": v(88.9, -215.9) * mm});
            skLineSegment(sketch, "E115.MirrorCS", {"start": v(95.25, -215.9) * mm, "end": v(95.25, -222.25) * mm});
            skLineSegment(sketch, "E116.MirrorCS", {"start": v(88.9, -215.9) * mm, "end": v(88.9, -222.25) * mm});
            skPoint(sketch, "E117.MirrorP", {"position": v(92.08, -222.25) * mm});
            skLineSegment(sketch, "E118.MirrorCS", {"start": v(82.55, -228.6) * mm, "end": v(114.3, -228.6) * mm});
            skArc(sketch, "E119.MirrorCS", {"start": v(114.3, -197.97) * mm, "mid": v(98.72, -206.19) * mm, "end": v(82.55, -213.17) * mm});
            skPoint(sketch, "E120.MirrorP", {"position": v(103.19, -214.31) * mm});
            skLineSegment(sketch, "E121.MirrorCS", {"start": v(82.55, -228.6) * mm, "end": v(82.55, -213.17) * mm});
            skPoint(sketch, "E122.MirrorP", {"position": v(93.66, -214.31) * mm});
            skLineSegment(sketch, "E123.MirrorCS", {"start": v(114.3, -228.6) * mm, "end": v(114.3, -197.97) * mm});
            skLineSegment(sketch, "E124.0", {"start": v(92.08, -212.72) * mm, "end": v(95.25, -215.9) * mm});
            skLineSegment(sketch, "E125.0", {"start": v(-92.08, -212.72) * mm, "end": v(-95.25, -215.9) * mm});
            skSolve(sketch);
        }
        {
            var Q0;
            Q0=makeQuery(id+"F17.imprint","IMPRINT",FACE,{"disambiguationData":[TD([[makeQuery(id+"F17.imprint","IMPRINT",EDGE,{"derivedFrom":sQuery(id+"F17.wireOp",EDGE,"E94")}),-1.0]])]});
            var Q1;
            Q1=makeQuery(id+"F17.imprint","IMPRINT",FACE,{"disambiguationData":[TD([[makeQuery(id+"F17.imprint","IMPRINT",EDGE,{"derivedFrom":sQuery(id+"F17.wireOp",EDGE,"E109.MirrorCS")}),-1.0]])]});
            extrude(context, id + "F18", {"entities" : qUnion([Q0, Q1]), "operationType" : NewBodyOperationType.ADD, "depth" : 12.7 * mm, "offsetDistance" : 25.4 * mm});
        }
    });
